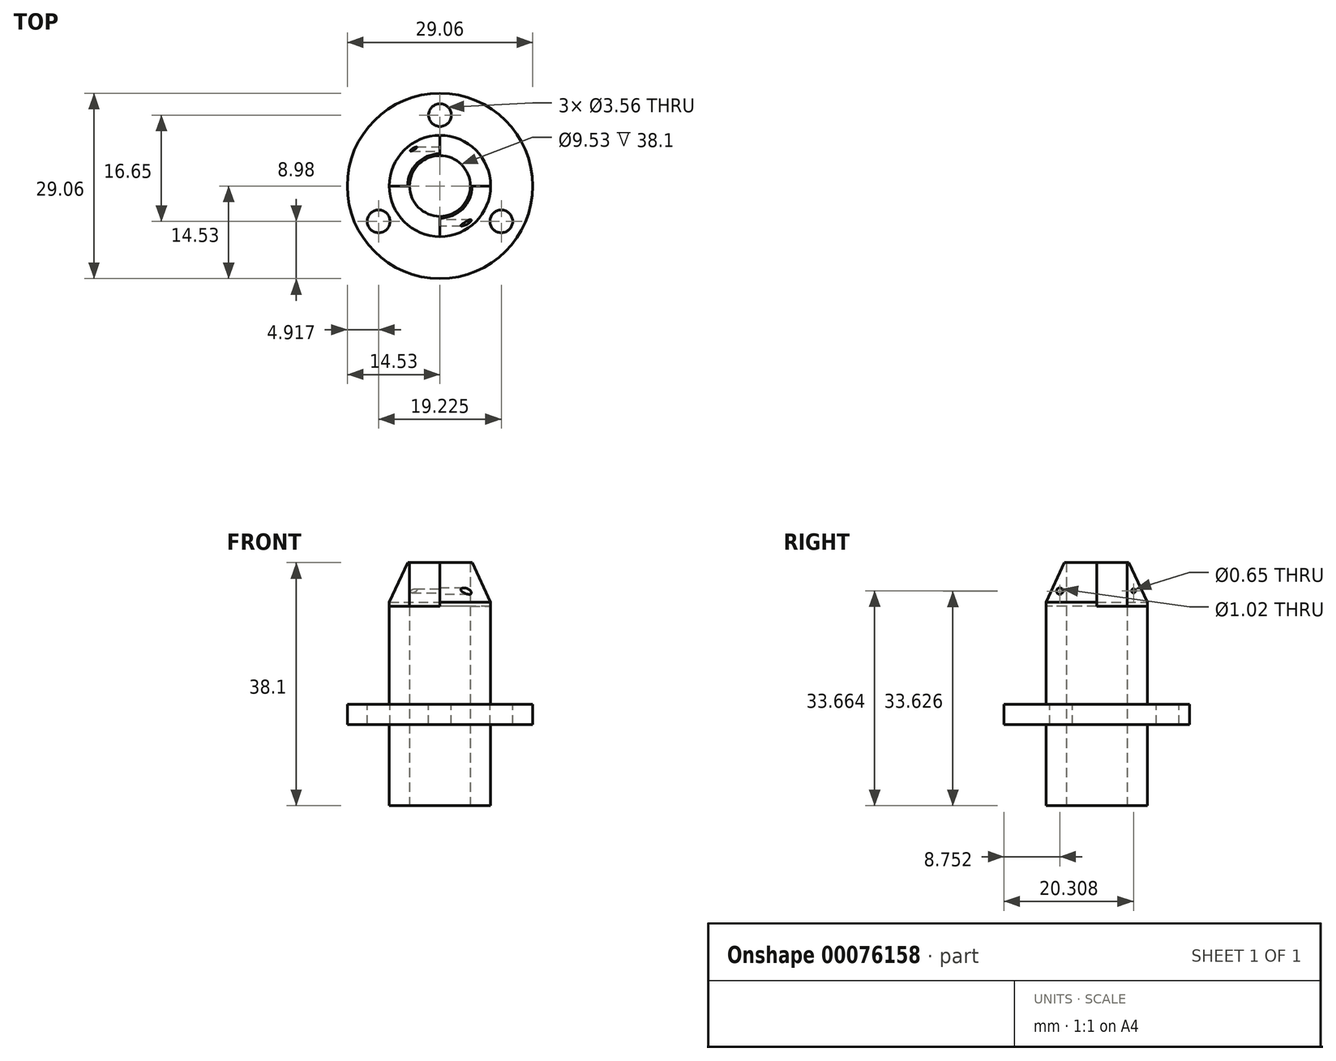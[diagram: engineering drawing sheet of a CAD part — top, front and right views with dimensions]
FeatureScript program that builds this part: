
annotation { "Feature Type Name" : "Feature", "Feature Type Description" : "" }
export const myFeature = defineFeature(function(context is Context, id is Id, definition is map)
    precondition{}
    {
        {
            var Q0;
            Q0=qCreatedBy(makeId("Top.planeOp"),FACE);
            var sketch = newSketch(context, id + "F0", { "sketchPlane" : qUnion([Q0])});
            skCircle(sketch, "E0", {"center": v(0, 0) * mm, "radius": 7.94 * mm});
            skCircle(sketch, "E1", {"center": v(0, 0) * mm, "radius": 4.76 * mm});
            skSolve(sketch);
        }
        {
            var Q0;
            Q0 = qSketchRegion(id + "F0", true);
            extrude(context, id + "F1", {"entities" : qUnion([Q0]), "depth" : 25.4 * mm, "hasSecondDirection" : true, "secondDirectionOppositeDirection" : true, "secondDirectionDepth" : 12.7 * mm});
        }
        {
            var Q0;
            Q0=makeQuery(id+"F1.opExtrude","CAP_FACE",FACE,{"disambiguationData":[OSD([sQuery(id+"F0.wireOp",EDGE,"E0"),sQuery(id+"F0.wireOp",EDGE,"E1")])],"isStart":false});
            var sketch = newSketch(context, id + "F2", { "sketchPlane" : qUnion([Q0])});
            skArc(sketch, "E2", {"start": v(-10.6, 0) * mm, "mid": v(-7.5, -7.5) * mm, "end": v(0, -10.6) * mm});
            skArc(sketch, "E3", {"start": v(-2.6, 0) * mm, "mid": v(-1.84, -1.84) * mm, "end": v(0, -2.6) * mm});
            skLineSegment(sketch, "E4", {"start": v(-10.6, 0) * mm, "end": v(-2.6, 0) * mm});
            skLineSegment(sketch, "E5", {"start": v(0, -2.6) * mm, "end": v(0, -10.6) * mm});
            skLineSegment(sketch, "E6", {"start": v(2.6, 0) * mm, "end": v(10.6, 0) * mm});
            skLineSegment(sketch, "E7", {"start": v(0, 2.6) * mm, "end": v(0, 10.6) * mm});
            skArc(sketch, "E8.trimOffspring", {"start": v(2.6, 0) * mm, "mid": v(1.84, 1.84) * mm, "end": v(0, 2.6) * mm});
            skArc(sketch, "E9.trimOffspring", {"start": v(10.6, 0) * mm, "mid": v(7.5, 7.5) * mm, "end": v(0, 10.6) * mm});
            skSolve(sketch);
        }
        {
            var Q0;
            Q0 = qSketchRegion(id + "F2", true);
            extrude(context, id + "F3", {"entities" : qUnion([Q0]), "operationType" : NewBodyOperationType.REMOVE, "oppositeDirection" : true, "depth" : 6.86 * mm});
        }
        {
            var Q0;
            {var subQ0=sQuery(id+"F0.wireOp",EDGE,"E0");var subQ1=sQuery(id+"F0.wireOp",EDGE,"E1");Q0=makeQuery(id+"F3.boolean.opBoolean","SPLIT",FACE,{"disambiguationData":[TD([makeQuery(id+"F3.opExtrude","SWEPT_FACE",FACE,{"disambiguationData":[OSD([sQuery(id+"F2.wireOp",EDGE,"E5")])]})])],"derivedFrom":makeQuery(id+"F1.opExtrude","CAP_FACE",FACE,{"disambiguationData":[OSD([subQ0,subQ1])],"isStart":false})});}
            var sketch = newSketch(context, id + "F4", { "sketchPlane" : qUnion([Q0])});
            skCircle(sketch, "E10", {"center": v(0, 0) * mm, "radius": 5.05 * mm});
            skCircle(sketch, "E11", {"center": v(0, 0) * mm, "radius": 11.42 * mm});
            skSolve(sketch);
        }
        {
            var Q0;
            Q0 = qSketchRegion(id + "F4", true);
            extrude(context, id + "F5", {"entities" : qUnion([Q0]), "operationType" : NewBodyOperationType.REMOVE, "oppositeDirection" : true, "depth" : 7.82 * mm, "hasDraft" : true, "draftAngle" : 25 * degree, "draftPullDirection" : true});
        }
        {
            var Q0;
            Q0=qCreatedBy(makeId("Top.planeOp"),FACE);
            var sketch = newSketch(context, id + "F6", { "sketchPlane" : qUnion([Q0])});
            skCircle(sketch, "E12", {"center": v(0, 0) * mm, "radius": 14.53 * mm});
            skCircle(sketch, "E13", {"center": v(0, 0) * mm, "radius": 4.76 * mm});
            skSolve(sketch);
        }
        {
            var Q0;
            Q0 = qSketchRegion(id + "F6", true);
            extrude(context, id + "F7", {"entities" : qUnion([Q0]), "operationType" : NewBodyOperationType.ADD, "depth" : 3.17 * mm});
        }
        {
            var Q0;
            Q0=makeQuery(id+"F7.opExtrude","CAP_FACE",FACE,{"disambiguationData":[OSD([sQuery(id+"F6.wireOp",EDGE,"E12"),sQuery(id+"F6.wireOp",EDGE,"E13")])],"isStart":false});
            var sketch = newSketch(context, id + "F8", { "sketchPlane" : qUnion([Q0])});
            skCircle(sketch, "E14", {"center": v(0, 11.1) * mm, "radius": 1.78 * mm});
            skCircle(sketch, "E15.1.0", {"center": v(-9.61, -5.55) * mm, "radius": 1.78 * mm});
            skCircle(sketch, "E15.2.0", {"center": v(9.61, -5.55) * mm, "radius": 1.78 * mm});
            skPoint(sketch, "E15.center", {"position": v(0, 0) * mm});
            skSolve(sketch);
        }
        {
            var Q0;
            Q0=makeQuery(id+"F8.imprint","IMPRINT",FACE,{"disambiguationData":[TD([[makeQuery(id+"F8.imprint","IMPRINT",EDGE,{"derivedFrom":sQuery(id+"F8.wireOp",EDGE,"E14")}),1.0]])]});
            var Q1;
            Q1=makeQuery(id+"F8.imprint","IMPRINT",FACE,{"disambiguationData":[TD([[makeQuery(id+"F8.imprint","IMPRINT",EDGE,{"derivedFrom":sQuery(id+"F8.wireOp",EDGE,"E15.2.0")}),1.0]])]});
            var Q2;
            Q2=makeQuery(id+"F8.imprint","IMPRINT",FACE,{"disambiguationData":[TD([[makeQuery(id+"F8.imprint","IMPRINT",EDGE,{"derivedFrom":sQuery(id+"F8.wireOp",EDGE,"E15.1.0")}),1.0]])]});
            extrude(context, id + "F9", {"entities" : qUnion([Q0, Q1, Q2]), "operationType" : NewBodyOperationType.REMOVE, "endBound" : BoundingType.THROUGH_ALL, "oppositeDirection" : true, "depth" : 25.4 * mm});
        }
        {
            var Q0;
            Q0=makeQuery(id+"F3.boolean.opBoolean","COPY",FACE,{"derivedFrom":makeQuery(id+"F3.opExtrude","SWEPT_FACE",FACE,{"disambiguationData":[OSD([sQuery(id+"F2.wireOp",EDGE,"E7")])]})});
            var sketch = newSketch(context, id + "F10", { "sketchPlane" : qUnion([Q0])});
            skCircle(sketch, "E16", {"center": v(5.78, 20.96) * mm, "radius": 0.33 * mm});
            skSolve(sketch);
        }
        {
            var Q0;
            Q0 = qSketchRegion(id + "F10", true);
            extrude(context, id + "F11", {"entities" : qUnion([Q0]), "operationType" : NewBodyOperationType.REMOVE, "oppositeDirection" : true, "depth" : 25.4 * mm});
        }
        {
            var Q0;
            Q0=makeQuery(id+"F3.boolean.opBoolean","COPY",FACE,{"derivedFrom":makeQuery(id+"F3.opExtrude","SWEPT_FACE",FACE,{"disambiguationData":[OSD([sQuery(id+"F2.wireOp",EDGE,"E5")])]})});
            var sketch = newSketch(context, id + "F12", { "sketchPlane" : qUnion([Q0])});
            skLineSegment(sketch, "E17", {"start": v(4.76, 18.54) * mm, "end": v(7.94, 18.54) * mm});
            skCircle(sketch, "E18", {"center": v(5.78, 20.93) * mm, "radius": 0.5 * mm});
            skSolve(sketch);
        }
        {
            var Q0;
            Q0 = qSketchRegion(id + "F12", true);
            extrude(context, id + "F13", {"entities" : qUnion([Q0]), "operationType" : NewBodyOperationType.REMOVE, "oppositeDirection" : true, "depth" : 25.4 * mm});
        }
    });
